AUTODESK INVENTOR PART (.ipt)
format: ipt  version: 2017 (Build 210142000, 142)  size: 427,520 bytes
history: native  units: mm (DEFAULTED — no unit token found)
features: other x104, plane x15, sketch x15, sweep x15
ambient origin geometry x8: Origin, YZ Plane, XZ Plane, XY Plane, X Axis, Y Axis, Z Axis, Center Point
bodies: Body1 (feature_tree), Body2 (feature_tree), Body3 (feature_tree)
feature tree (149):
  other  "Work Point1"
  other  "Work Point2"
  other  "Wire1"
  other  "Work Point3"
  other  "Work Point4"
  other  "Wire2"
  other  "Work Point5"
  other  "Work Point6"
  other  "Wire3"
  other  "Work Point7"
  other  "Work Point8"
  other  "Wire4"
  other  "Work Point9"
  other  "Work Point10"
  other  "Wire5"
  other  "Work Point11"
  other  "Work Point12"
  other  "Wire6"
  other  "Work Point13"
  other  "Work Point14"
  other  "Wire7"
  other  "Work Point15"
  other  "Work Point16"
  other  "Wire8"
  other  "Work Point17"
  other  "Work Point18"
  other  "Wire9"
  other  "Work Point19"
  other  "Work Point20"
  other  "Wire10"
  other  "Work Point21"
  other  "Work Point22"
  other  "Wire11"
  other  "Work Point23"
  other  "Work Point24"
  other  "Wire12"
  other  "Work Point25"
  other  "Work Point26"
  other  "Wire13"
  other  "Work Point27"
  other  "Work Point28"
  other  "Wire14"
  other  "Work Point29"
  other  "Work Point30"
  other  "Wire15"
  other  "Work Point31"
  other  "Work Point32"
  other  "Wire16"
  other  "Work Point33"
  other  "Work Point34"
  other  "Wire17"
  other  "Work Point35"
  other  "Work Point36"
  other  "Wire18"
  plane  "Work Plane6"
  plane  "Work Plane7"
  plane  "Work Plane8"
  plane  "Work Plane9"
  plane  "Work Plane10"
  plane  "Work Plane11"
  plane  "Work Plane12"
  plane  "Work Plane13"
  plane  "Work Plane14"
  plane  "Work Plane15"
  plane  "Work Plane16"
  plane  "Work Plane17"
  other  "Work Point61"
  other  "Work Point62"
  other  "Segment1"
  other  "Work Point63"
  other  "Work Point64"
  other  "Work Point65"
  other  "Work Point66"
  other  "Work Point67"
  other  "Work Point68"
  other  "Work Point69"
  other  "Work Point70"
  other  "Work Point71"
  other  "Work Point72"
  other  "Segment2"
  other  "Work Point73"
  other  "Work Point74"
  other  "Work Point75"
  other  "Work Point76"
  plane  "Work Plane19"
  plane  "Work Plane20"
  other  "Work Point77"
  other  "Work Point78"
  other  "Segment3"
  other  "Work Point79"
  other  "Work Point80"
  other  "Work Point81"
  other  "Work Point82"
  other  "Work Point83"
  other  "Work Point84"
  other  "Work Point85"
  other  "Work Point86"
  other  "Work Point87"
  other  "Work Point88"
  other  "Work Point89"
  other  "Work Point90"
  other  "Work Point91"
  other  "Work Point92"
  plane  "Work Plane21"
  sketch  "Sketch6"  dims[d10=0.0mm d11=0.0mm d12=0.0mm d13=0.0mm]
  other  "Srf6"
  sketch  "Sketch7"  dims[d14=0.0mm d15=0.0mm d16=0.0mm d17=0.0mm]
  other  "Srf7"
  sketch  "Sketch8"  dims[d18=0.0mm d19=0.0mm d20=0.0mm d21=0.0mm]
  other  "Srf8"
  sketch  "Sketch9"  dims[d22=0.0mm d23=0.0mm d24=0.0mm d25=0.0mm]
  other  "Srf9"
  sketch  "Sketch10"  dims[d26=0.0mm d27=0.0mm d28=0.0mm d29=0.0mm]
  other  "Srf10"
  sketch  "Sketch11"  dims[d30=0.0mm d31=0.0mm d32=0.0mm d33=0.0mm]
  other  "Srf11"
  sketch  "Sketch12"  dims[d36=0.0mm d37=0.0mm d38=0.0mm d39=0.0mm]
  other  "Srf12"
  sketch  "Sketch13"  dims[d40=0.0mm d41=0.0mm]
  other  "Srf13"
  sketch  "Sketch14"
  other  "Srf14"
  sketch  "Sketch15"
  other  "Srf15"
  sketch  "Sketch16"
  other  "Srf16"
  sketch  "Sketch17"
  other  "Srf17"
  sketch  "Sketch19"
  other  "Srf19"
  sketch  "Sketch20"
  other  "Srf20"
  sketch  "Sketch21"
  other  "Srf21"
  sweep  "SweepSrf6"
  sweep  "SweepSrf7"
  sweep  "SweepSrf8"
  sweep  "SweepSrf9"
  sweep  "SweepSrf10"
  sweep  "SweepSrf11"
  sweep  "SweepSrf12"
  sweep  "SweepSrf13"
  sweep  "SweepSrf14"
  sweep  "SweepSrf15"
  sweep  "SweepSrf16"
  sweep  "SweepSrf17"
  sweep  "SweepSrf19"
  sweep  "SweepSrf20"
  sweep  "SweepSrf21"
